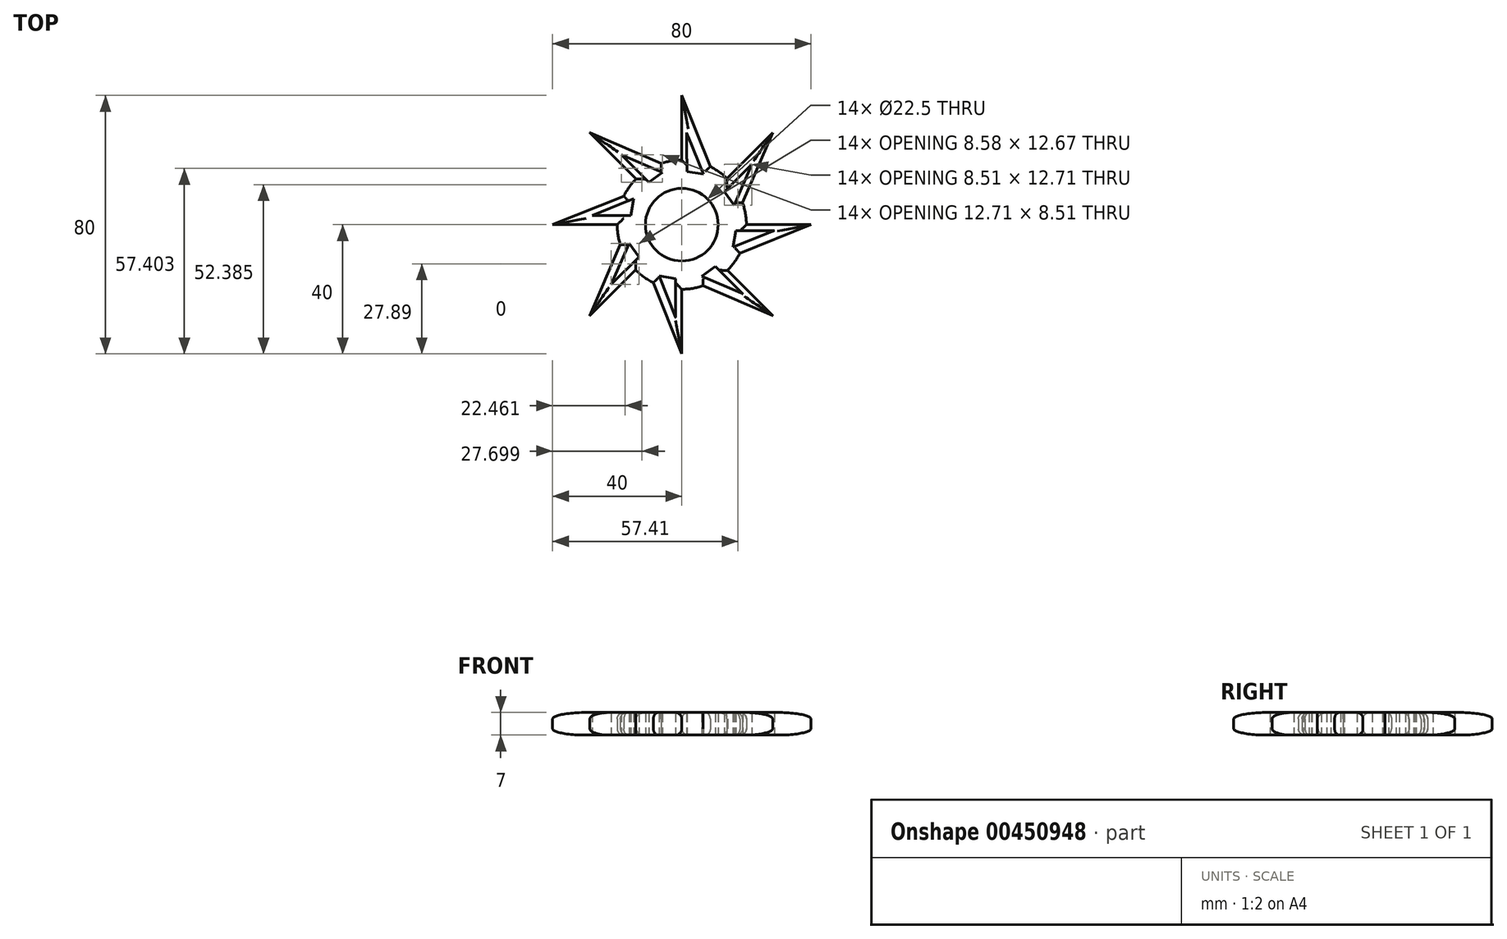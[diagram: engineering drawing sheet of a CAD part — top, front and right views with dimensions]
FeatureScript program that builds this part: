
annotation { "Feature Type Name" : "Feature", "Feature Type Description" : "" }
export const myFeature = defineFeature(function(context is Context, id is Id, definition is map)
    precondition{}
    {
        {
            var Q0;
            Q0=qCreatedBy(makeId("Top.planeOp"),FACE);
            var sketch = newSketch(context, id + "F0", { "sketchPlane" : qUnion([Q0])});
            skCircle(sketch, "E0", {"center": v(0, 0) * mm, "radius": 16 * mm});
            skCircle(sketch, "E1", {"center": v(0, 0) * mm, "radius": 11.25 * mm});
            skCircle(sketch, "E2", {"center": v(0, 0) * mm, "radius": 40 * mm});
            skLineSegment(sketch, "E3", {"start": v(0, 16) * mm, "end": v(0, 40) * mm});
            skLineSegment(sketch, "E4", {"start": v(0, 40) * mm, "end": v(16, 0) * mm});
            skLineSegment(sketch, "E5", {"start": v(16, 0) * mm, "end": v(40, 0) * mm});
            skLineSegment(sketch, "E6", {"start": v(40, 0) * mm, "end": v(0, -16) * mm});
            skLineSegment(sketch, "E7", {"start": v(0, -16) * mm, "end": v(0, -40) * mm});
            skLineSegment(sketch, "E8", {"start": v(0, -40) * mm, "end": v(-16, 0) * mm});
            skLineSegment(sketch, "E9", {"start": v(-16, 0) * mm, "end": v(-40, 0) * mm});
            skLineSegment(sketch, "E10", {"start": v(-40, 0) * mm, "end": v(0, 16) * mm});
            skLineSegment(sketch, "E11", {"start": v(-11.48, 11.48) * mm, "end": v(-28.45, 28.45) * mm});
            skLineSegment(sketch, "E12", {"start": v(-28.45, 28.45) * mm, "end": v(11.15, 11.48) * mm});
            skLineSegment(sketch, "E13", {"start": v(11.15, 11.48) * mm, "end": v(28.12, 28.45) * mm});
            skLineSegment(sketch, "E14", {"start": v(28.12, 28.45) * mm, "end": v(11.15, -11.15) * mm});
            skLineSegment(sketch, "E15", {"start": v(11.15, -11.15) * mm, "end": v(28.12, -28.12) * mm});
            skLineSegment(sketch, "E16", {"start": v(28.12, -28.12) * mm, "end": v(-11.48, -11.15) * mm});
            skLineSegment(sketch, "E17", {"start": v(-11.48, -11.15) * mm, "end": v(-28.45, -28.12) * mm});
            skLineSegment(sketch, "E18", {"start": v(-28.45, -28.12) * mm, "end": v(-11.48, 11.48) * mm});
            skCircle(sketch, "E19", {"center": v(0, 0) * mm, "radius": 20 * mm});
            skLineSegment(sketch, "E20", {"start": v(-14.94, 8) * mm, "end": v(-27.78, 2.86) * mm});
            skPoint(sketch, "E20.startSnap0", {"position": v(-20, 8) * mm});
            skLineSegment(sketch, "E21", {"start": v(-27.78, 2.86) * mm, "end": v(-15.74, 2.86) * mm});
            skLineSegment(sketch, "E22", {"start": v(-15.74, 2.86) * mm, "end": v(-14.94, 8) * mm});
            skLineSegment(sketch, "E23", {"start": v(-5.94, 16.21) * mm, "end": v(-18.66, 21.66) * mm});
            skLineSegment(sketch, "E24", {"start": v(-18.66, 21.66) * mm, "end": v(-10.15, 13.15) * mm});
            skLineSegment(sketch, "E25", {"start": v(-10.15, 13.15) * mm, "end": v(-5.94, 16.21) * mm});
            skLineSegment(sketch, "E26", {"start": v(6.72, 15.65) * mm, "end": v(1.49, 28.45) * mm});
            skLineSegment(sketch, "E27", {"start": v(1.49, 28.45) * mm, "end": v(1.58, 16.42) * mm});
            skLineSegment(sketch, "E28", {"start": v(1.58, 16.42) * mm, "end": v(6.72, 15.65) * mm});
            skLineSegment(sketch, "E29", {"start": v(16.22, 6.03) * mm, "end": v(21.67, 18.74) * mm});
            skLineSegment(sketch, "E30", {"start": v(21.67, 18.74) * mm, "end": v(13.15, 10.23) * mm});
            skLineSegment(sketch, "E31", {"start": v(13.15, 10.23) * mm, "end": v(16.22, 6.03) * mm});
            skLineSegment(sketch, "E32", {"start": v(15.88, -6.94) * mm, "end": v(28.72, -1.8) * mm});
            skLineSegment(sketch, "E33", {"start": v(28.72, -1.8) * mm, "end": v(16.68, -1.8) * mm});
            skLineSegment(sketch, "E34", {"start": v(16.68, -1.8) * mm, "end": v(15.88, -6.94) * mm});
            skLineSegment(sketch, "E35", {"start": v(6.15, -15.96) * mm, "end": v(18.86, -21.4) * mm});
            skLineSegment(sketch, "E36", {"start": v(18.86, -21.4) * mm, "end": v(10.35, -12.9) * mm});
            skLineSegment(sketch, "E37", {"start": v(10.35, -12.9) * mm, "end": v(6.15, -15.96) * mm});
            skLineSegment(sketch, "E38", {"start": v(-7.01, -15.84) * mm, "end": v(-1.96, -28.72) * mm});
            skLineSegment(sketch, "E39", {"start": v(-1.96, -28.72) * mm, "end": v(-1.88, -16.68) * mm});
            skLineSegment(sketch, "E40", {"start": v(-1.88, -16.68) * mm, "end": v(-7.01, -15.84) * mm});
            skLineSegment(sketch, "E41", {"start": v(-16.28, -5.78) * mm, "end": v(-21.83, -18.44) * mm});
            skLineSegment(sketch, "E42", {"start": v(-21.83, -18.44) * mm, "end": v(-13.25, -10) * mm});
            skLineSegment(sketch, "E43", {"start": v(-13.25, -10) * mm, "end": v(-16.28, -5.78) * mm});
            skSolve(sketch);
        }
        {
            var Q0;
            {var subQ0=sQuery(id+"F0.wireOp",EDGE,"E14");var subQ1=sQuery(id+"F0.wireOp",EDGE,"E2");var subQ2=makeQuery(id+"F0.imprint","INTERSECT",VERTEX,{"derivedFrom":[subQ1,subQ0]});Q0=makeQuery(id+"F0.imprint","IMPRINT",FACE,{"disambiguationData":[TD([[makeQuery(id+"F0.imprint","IMPRINT",EDGE,{"disambiguationData":[TD([[subQ2,-1.0]])],"derivedFrom":subQ1}),-1.0]])]});}
            var Q1;
            {var subQ0=sQuery(id+"F0.wireOp",EDGE,"E12");var subQ1=sQuery(id+"F0.wireOp",EDGE,"E2");var subQ2=makeQuery(id+"F0.imprint","INTERSECT",VERTEX,{"derivedFrom":[subQ1,subQ0]});Q1=makeQuery(id+"F0.imprint","IMPRINT",FACE,{"disambiguationData":[TD([[makeQuery(id+"F0.imprint","IMPRINT",EDGE,{"disambiguationData":[TD([[subQ2,-1.0]])],"derivedFrom":subQ1}),-1.0]])]});}
            var Q2;
            {var subQ0=sQuery(id+"F0.wireOp",EDGE,"E19");var subQ5=sQuery(id+"F0.wireOp",EDGE,"E4");var subQ6=makeQuery(id+"F0.imprint","INTERSECT",VERTEX,{"derivedFrom":[subQ5,subQ0]});Q2=makeQuery(id+"F0.imprint","IMPRINT",FACE,{"disambiguationData":[TD([[makeQuery(id+"F0.imprint","IMPRINT",EDGE,{"disambiguationData":[TD([[subQ6,-1.0]])],"derivedFrom":subQ0}),-1.0]])]});}
            var Q3;
            {var subQ0=sQuery(id+"F0.wireOp",EDGE,"E19");var subQ1=sQuery(id+"F0.wireOp",EDGE,"E6");var subQ2=makeQuery(id+"F0.imprint","INTERSECT",VERTEX,{"derivedFrom":[subQ1,subQ0]});Q3=makeQuery(id+"F0.imprint","IMPRINT",FACE,{"disambiguationData":[TD([[makeQuery(id+"F0.imprint","IMPRINT",EDGE,{"disambiguationData":[TD([[subQ2,-1.0]])],"derivedFrom":subQ0}),-1.0]])]});}
            var Q4;
            {var subQ0=sQuery(id+"F0.wireOp",EDGE,"E19");var subQ1=sQuery(id+"F0.wireOp",EDGE,"E8");var subQ2=makeQuery(id+"F0.imprint","INTERSECT",VERTEX,{"derivedFrom":[subQ1,subQ0]});Q4=makeQuery(id+"F0.imprint","IMPRINT",FACE,{"disambiguationData":[TD([[makeQuery(id+"F0.imprint","IMPRINT",EDGE,{"disambiguationData":[TD([[subQ2,-1.0]])],"derivedFrom":subQ0}),-1.0]])]});}
            var Q5;
            {var subQ0=sQuery(id+"F0.wireOp",EDGE,"E19");var subQ1=sQuery(id+"F0.wireOp",EDGE,"E18");var subQ2=makeQuery(id+"F0.imprint","INTERSECT",VERTEX,{"derivedFrom":[subQ1,subQ0]});Q5=makeQuery(id+"F0.imprint","IMPRINT",FACE,{"disambiguationData":[TD([[makeQuery(id+"F0.imprint","IMPRINT",EDGE,{"disambiguationData":[TD([[subQ2,-1.0]])],"derivedFrom":subQ0}),-1.0]])]});}
            var Q6;
            {var subQ1=sQuery(id+"F0.wireOp",EDGE,"E14");var subQ6=sQuery(id+"F0.wireOp",EDGE,"E2");var subQ9=makeQuery(id+"F0.imprint","INTERSECT",VERTEX,{"derivedFrom":[subQ6,subQ1]});Q6=makeQuery(id+"F0.imprint","IMPRINT",FACE,{"disambiguationData":[TD([[makeQuery(id+"F0.imprint","IMPRINT",EDGE,{"disambiguationData":[TD([[subQ9,-1.0]])],"derivedFrom":subQ6}),1.0]])]});}
            var Q7;
            {var subQ1=sQuery(id+"F0.wireOp",EDGE,"E12");var subQ6=sQuery(id+"F0.wireOp",EDGE,"E2");var subQ9=makeQuery(id+"F0.imprint","INTERSECT",VERTEX,{"derivedFrom":[subQ6,subQ1]});Q7=makeQuery(id+"F0.imprint","IMPRINT",FACE,{"disambiguationData":[TD([[makeQuery(id+"F0.imprint","IMPRINT",EDGE,{"disambiguationData":[TD([[subQ9,-1.0]])],"derivedFrom":subQ6}),1.0]])]});}
            var Q8;
            {var subQ0=sQuery(id+"F0.wireOp",EDGE,"E19");var subQ1=sQuery(id+"F0.wireOp",EDGE,"E10");var subQ2=makeQuery(id+"F0.imprint","INTERSECT",VERTEX,{"derivedFrom":[subQ1,subQ0]});Q8=makeQuery(id+"F0.imprint","IMPRINT",FACE,{"disambiguationData":[TD([[makeQuery(id+"F0.imprint","IMPRINT",EDGE,{"disambiguationData":[TD([[subQ2,-1.0]])],"derivedFrom":subQ0}),-1.0]])]});}
            var Q9;
            {var subQ1=sQuery(id+"F0.wireOp",EDGE,"E15");var subQ5=sQuery(id+"F0.wireOp",EDGE,"E16");var subQ6=makeQuery(id+"F0.imprint","INTERSECT",VERTEX,{"derivedFrom":[subQ1,subQ5]});Q9=makeQuery(id+"F0.imprint","IMPRINT",FACE,{"disambiguationData":[TD([[makeQuery(id+"F0.imprint","IMPRINT",EDGE,{"disambiguationData":[TD([[subQ6,1.0]])],"derivedFrom":subQ1}),-1.0]])]});}
            var Q10;
            {var subQ5=sQuery(id+"F0.wireOp",EDGE,"E37");Q10=makeQuery(id+"F0.imprint","IMPRINT",FACE,{"disambiguationData":[TD([[makeQuery(id+"F0.imprint","IMPRINT",EDGE,{"derivedFrom":subQ5}),-1.0]])]});}
            var Q11;
            {var subQ0=sQuery(id+"F0.wireOp",EDGE,"E40");Q11=makeQuery(id+"F0.imprint","IMPRINT",FACE,{"disambiguationData":[TD([[makeQuery(id+"F0.imprint","IMPRINT",EDGE,{"derivedFrom":subQ0}),-1.0]])]});}
            var Q12;
            {var subQ0=sQuery(id+"F0.wireOp",EDGE,"E16");var subQ1=sQuery(id+"F0.wireOp",EDGE,"E7");var subQ2=makeQuery(id+"F0.imprint","INTERSECT",VERTEX,{"derivedFrom":[subQ1,subQ0]});Q12=makeQuery(id+"F0.imprint","IMPRINT",FACE,{"disambiguationData":[TD([[makeQuery(id+"F0.imprint","IMPRINT",EDGE,{"disambiguationData":[TD([[subQ2,-1.0]])],"derivedFrom":subQ1}),1.0]])]});}
            var Q13;
            {var subQ0=sQuery(id+"F0.wireOp",EDGE,"E19");var subQ1=sQuery(id+"F0.wireOp",EDGE,"E6");var subQ2=makeQuery(id+"F0.imprint","INTERSECT",VERTEX,{"derivedFrom":[subQ1,subQ0]});Q13=makeQuery(id+"F0.imprint","IMPRINT",FACE,{"disambiguationData":[TD([[makeQuery(id+"F0.imprint","IMPRINT",EDGE,{"disambiguationData":[TD([[subQ2,-1.0]])],"derivedFrom":subQ1}),1.0]])]});}
            var Q14;
            {var subQ1=sQuery(id+"F0.wireOp",EDGE,"E0");var subQ3=sQuery(id+"F0.wireOp",EDGE,"E14");var subQ4=makeQuery(id+"F0.imprint","INTERSECT",VERTEX,{"derivedFrom":[subQ1,subQ3]});Q14=makeQuery(id+"F0.imprint","IMPRINT",FACE,{"disambiguationData":[TD([[makeQuery(id+"F0.imprint","IMPRINT",EDGE,{"disambiguationData":[TD([[subQ4,1.0]])],"derivedFrom":subQ3}),1.0]])]});}
            var Q15;
            {var subQ3=sQuery(id+"F0.wireOp",EDGE,"E15");var subQ5=sQuery(id+"F0.wireOp",EDGE,"E14");var subQ7=makeQuery(id+"F0.imprint","INTERSECT",VERTEX,{"derivedFrom":[subQ5,subQ3]});Q15=makeQuery(id+"F0.imprint","IMPRINT",FACE,{"disambiguationData":[TD([[makeQuery(id+"F0.imprint","IMPRINT",EDGE,{"disambiguationData":[TD([[subQ7,1.0]])],"derivedFrom":subQ5}),1.0]])]});}
            var Q16;
            {var subQ0=sQuery(id+"F0.wireOp",EDGE,"E6");var subQ1=sQuery(id+"F0.wireOp",EDGE,"E0");var subQ3=makeQuery(id+"F0.imprint","INTERSECT",VERTEX,{"derivedFrom":[subQ1,subQ0]});Q16=makeQuery(id+"F0.imprint","IMPRINT",FACE,{"disambiguationData":[TD([[makeQuery(id+"F0.imprint","IMPRINT",EDGE,{"disambiguationData":[TD([[subQ3,1.0]])],"derivedFrom":subQ1}),1.0]])]});}
            var Q17;
            {var subQ0=sQuery(id+"F0.wireOp",EDGE,"E16");var subQ1=sQuery(id+"F0.wireOp",EDGE,"E0");var subQ2=makeQuery(id+"F0.imprint","INTERSECT",VERTEX,{"disambiguationData":[OD(0.0)],"derivedFrom":[subQ1,subQ0]});Q17=makeQuery(id+"F0.imprint","IMPRINT",FACE,{"disambiguationData":[TD([[makeQuery(id+"F0.imprint","IMPRINT",EDGE,{"disambiguationData":[TD([[subQ2,-1.0]])],"derivedFrom":subQ1}),1.0]])]});}
            var Q18;
            {var subQ0=sQuery(id+"F0.wireOp",EDGE,"E19");var subQ1=sQuery(id+"F0.wireOp",EDGE,"E8");var subQ2=makeQuery(id+"F0.imprint","INTERSECT",VERTEX,{"derivedFrom":[subQ1,subQ0]});Q18=makeQuery(id+"F0.imprint","IMPRINT",FACE,{"disambiguationData":[TD([[makeQuery(id+"F0.imprint","IMPRINT",EDGE,{"disambiguationData":[TD([[subQ2,-1.0]])],"derivedFrom":subQ1}),1.0]])]});}
            var Q19;
            {var subQ0=sQuery(id+"F0.wireOp",EDGE,"E18");var subQ1=sQuery(id+"F0.wireOp",EDGE,"E9");var subQ2=makeQuery(id+"F0.imprint","INTERSECT",VERTEX,{"derivedFrom":[subQ1,subQ0]});Q19=makeQuery(id+"F0.imprint","IMPRINT",FACE,{"disambiguationData":[TD([[makeQuery(id+"F0.imprint","IMPRINT",EDGE,{"disambiguationData":[TD([[subQ2,-1.0]])],"derivedFrom":subQ1}),1.0]])]});}
            var Q20;
            {var subQ0=sQuery(id+"F0.wireOp",EDGE,"E19");var subQ1=sQuery(id+"F0.wireOp",EDGE,"E10");var subQ2=makeQuery(id+"F0.imprint","INTERSECT",VERTEX,{"derivedFrom":[subQ1,subQ0]});Q20=makeQuery(id+"F0.imprint","IMPRINT",FACE,{"disambiguationData":[TD([[makeQuery(id+"F0.imprint","IMPRINT",EDGE,{"disambiguationData":[TD([[subQ2,-1.0]])],"derivedFrom":subQ1}),1.0]])]});}
            var Q21;
            {var subQ0=sQuery(id+"F0.wireOp",EDGE,"E12");var subQ1=sQuery(id+"F0.wireOp",EDGE,"E3");var subQ2=makeQuery(id+"F0.imprint","INTERSECT",VERTEX,{"derivedFrom":[subQ1,subQ0]});Q21=makeQuery(id+"F0.imprint","IMPRINT",FACE,{"disambiguationData":[TD([[makeQuery(id+"F0.imprint","IMPRINT",EDGE,{"disambiguationData":[TD([[subQ2,-1.0]])],"derivedFrom":subQ1}),1.0]])]});}
            var Q22;
            {var subQ0=sQuery(id+"F0.wireOp",EDGE,"E19");var subQ1=sQuery(id+"F0.wireOp",EDGE,"E4");var subQ2=makeQuery(id+"F0.imprint","INTERSECT",VERTEX,{"derivedFrom":[subQ1,subQ0]});Q22=makeQuery(id+"F0.imprint","IMPRINT",FACE,{"disambiguationData":[TD([[makeQuery(id+"F0.imprint","IMPRINT",EDGE,{"disambiguationData":[TD([[subQ2,-1.0]])],"derivedFrom":subQ1}),1.0]])]});}
            var Q23;
            {var subQ0=sQuery(id+"F0.wireOp",EDGE,"E12");var subQ1=sQuery(id+"F0.wireOp",EDGE,"E0");var subQ2=makeQuery(id+"F0.imprint","INTERSECT",VERTEX,{"disambiguationData":[OD(0.0)],"derivedFrom":[subQ1,subQ0]});Q23=makeQuery(id+"F0.imprint","IMPRINT",FACE,{"disambiguationData":[TD([[makeQuery(id+"F0.imprint","IMPRINT",EDGE,{"disambiguationData":[TD([[subQ2,-1.0]])],"derivedFrom":subQ1}),1.0]])]});}
            var Q24;
            {var subQ0=sQuery(id+"F0.wireOp",EDGE,"E14");var subQ1=sQuery(id+"F0.wireOp",EDGE,"E0");var subQ2=makeQuery(id+"F0.imprint","INTERSECT",VERTEX,{"derivedFrom":[subQ1,subQ0]});Q24=makeQuery(id+"F0.imprint","IMPRINT",FACE,{"disambiguationData":[TD([[makeQuery(id+"F0.imprint","IMPRINT",EDGE,{"disambiguationData":[TD([[subQ2,-1.0]])],"derivedFrom":subQ1}),1.0]])]});}
            var Q25;
            {var subQ0=sQuery(id+"F0.wireOp",EDGE,"E10");var subQ1=sQuery(id+"F0.wireOp",EDGE,"E0");var subQ3=makeQuery(id+"F0.imprint","INTERSECT",VERTEX,{"derivedFrom":[subQ1,subQ0]});Q25=makeQuery(id+"F0.imprint","IMPRINT",FACE,{"disambiguationData":[TD([[makeQuery(id+"F0.imprint","IMPRINT",EDGE,{"disambiguationData":[TD([[subQ3,1.0]])],"derivedFrom":subQ1}),1.0]])]});}
            var Q26;
            {var subQ0=sQuery(id+"F0.wireOp",EDGE,"E0");var subQ2=sQuery(id+"F0.wireOp",EDGE,"E18");var subQ3=makeQuery(id+"F0.imprint","INTERSECT",VERTEX,{"disambiguationData":[OD(0.0)],"derivedFrom":[subQ0,subQ2]});Q26=makeQuery(id+"F0.imprint","IMPRINT",FACE,{"disambiguationData":[TD([[makeQuery(id+"F0.imprint","IMPRINT",EDGE,{"disambiguationData":[TD([[subQ3,1.0]])],"derivedFrom":subQ2}),1.0]])]});}
            var Q27;
            {var subQ0=sQuery(id+"F0.wireOp",EDGE,"E8");var subQ1=sQuery(id+"F0.wireOp",EDGE,"E0");var subQ3=makeQuery(id+"F0.imprint","INTERSECT",VERTEX,{"derivedFrom":[subQ1,subQ0]});Q27=makeQuery(id+"F0.imprint","IMPRINT",FACE,{"disambiguationData":[TD([[makeQuery(id+"F0.imprint","IMPRINT",EDGE,{"disambiguationData":[TD([[subQ3,1.0]])],"derivedFrom":subQ1}),1.0]])]});}
            var Q28;
            {var subQ1=sQuery(id+"F0.wireOp",EDGE,"E0");var subQ3=sQuery(id+"F0.wireOp",EDGE,"E18");var subQ4=makeQuery(id+"F0.imprint","INTERSECT",VERTEX,{"disambiguationData":[OD(1.0)],"derivedFrom":[subQ1,subQ3]});Q28=makeQuery(id+"F0.imprint","IMPRINT",FACE,{"disambiguationData":[TD([[makeQuery(id+"F0.imprint","IMPRINT",EDGE,{"disambiguationData":[TD([[subQ4,1.0]])],"derivedFrom":subQ3}),-1.0]])]});}
            var Q29;
            Q29=makeQuery(id+"F0.imprint","IMPRINT",FACE,{"disambiguationData":[TD([[makeQuery(id+"F0.imprint","IMPRINT",EDGE,{"derivedFrom":sQuery(id+"F0.wireOp",EDGE,"E1")}),-1.0]])]});
            var Q30;
            {var subQ0=sQuery(id+"F0.wireOp",EDGE,"E8");var subQ1=sQuery(id+"F0.wireOp",EDGE,"E0");var subQ2=makeQuery(id+"F0.imprint","INTERSECT",VERTEX,{"derivedFrom":[subQ1,subQ0]});Q30=makeQuery(id+"F0.imprint","IMPRINT",FACE,{"disambiguationData":[TD([[makeQuery(id+"F0.imprint","IMPRINT",EDGE,{"disambiguationData":[TD([[subQ2,-1.0]])],"derivedFrom":subQ1}),-1.0]])]});}
            var Q31;
            {var subQ1=sQuery(id+"F0.wireOp",EDGE,"E0");var subQ3=sQuery(id+"F0.wireOp",EDGE,"E16");var subQ4=makeQuery(id+"F0.imprint","INTERSECT",VERTEX,{"disambiguationData":[OD(1.0)],"derivedFrom":[subQ1,subQ3]});Q31=makeQuery(id+"F0.imprint","IMPRINT",FACE,{"disambiguationData":[TD([[makeQuery(id+"F0.imprint","IMPRINT",EDGE,{"disambiguationData":[TD([[subQ4,1.0]])],"derivedFrom":subQ3}),-1.0]])]});}
            var Q32;
            {var subQ0=sQuery(id+"F0.wireOp",EDGE,"E6");var subQ1=sQuery(id+"F0.wireOp",EDGE,"E0");var subQ2=makeQuery(id+"F0.imprint","INTERSECT",VERTEX,{"derivedFrom":[subQ1,subQ0]});Q32=makeQuery(id+"F0.imprint","IMPRINT",FACE,{"disambiguationData":[TD([[makeQuery(id+"F0.imprint","IMPRINT",EDGE,{"disambiguationData":[TD([[subQ2,-1.0]])],"derivedFrom":subQ1}),-1.0]])]});}
            var Q33;
            {var subQ1=sQuery(id+"F0.wireOp",EDGE,"E0");var subQ3=sQuery(id+"F0.wireOp",EDGE,"E14");var subQ4=makeQuery(id+"F0.imprint","INTERSECT",VERTEX,{"derivedFrom":[subQ1,subQ3]});Q33=makeQuery(id+"F0.imprint","IMPRINT",FACE,{"disambiguationData":[TD([[makeQuery(id+"F0.imprint","IMPRINT",EDGE,{"disambiguationData":[TD([[subQ4,-1.0]])],"derivedFrom":subQ3}),1.0]])]});}
            var Q34;
            {var subQ0=sQuery(id+"F0.wireOp",EDGE,"E4");var subQ1=sQuery(id+"F0.wireOp",EDGE,"E0");var subQ2=makeQuery(id+"F0.imprint","INTERSECT",VERTEX,{"derivedFrom":[subQ1,subQ0]});Q34=makeQuery(id+"F0.imprint","IMPRINT",FACE,{"disambiguationData":[TD([[makeQuery(id+"F0.imprint","IMPRINT",EDGE,{"disambiguationData":[TD([[subQ2,-1.0]])],"derivedFrom":subQ1}),-1.0]])]});}
            var Q35;
            {var subQ14=sQuery(id+"F0.wireOp",EDGE,"E34");Q35=makeQuery(id+"F0.imprint","IMPRINT",FACE,{"disambiguationData":[TD([[makeQuery(id+"F0.imprint","IMPRINT",EDGE,{"derivedFrom":subQ14}),-1.0]])]});}
            var Q36;
            {var subQ12=sQuery(id+"F0.wireOp",EDGE,"E31");Q36=makeQuery(id+"F0.imprint","IMPRINT",FACE,{"disambiguationData":[TD([[makeQuery(id+"F0.imprint","IMPRINT",EDGE,{"derivedFrom":subQ12}),-1.0]])]});}
            var Q37;
            {var subQ10=sQuery(id+"F0.wireOp",EDGE,"E43");Q37=makeQuery(id+"F0.imprint","IMPRINT",FACE,{"disambiguationData":[TD([[makeQuery(id+"F0.imprint","IMPRINT",EDGE,{"derivedFrom":subQ10}),-1.0]])]});}
            var Q38;
            {var subQ1=sQuery(id+"F0.wireOp",EDGE,"E9");var subQ5=sQuery(id+"F0.wireOp",EDGE,"E18");var subQ8=makeQuery(id+"F0.imprint","INTERSECT",VERTEX,{"derivedFrom":[subQ1,subQ5]});Q38=makeQuery(id+"F0.imprint","IMPRINT",FACE,{"disambiguationData":[TD([[makeQuery(id+"F0.imprint","IMPRINT",EDGE,{"disambiguationData":[TD([[subQ8,-1.0]])],"derivedFrom":subQ1}),-1.0]])]});}
            var Q39;
            {var subQ9=sQuery(id+"F0.wireOp",EDGE,"E22");Q39=makeQuery(id+"F0.imprint","IMPRINT",FACE,{"disambiguationData":[TD([[makeQuery(id+"F0.imprint","IMPRINT",EDGE,{"derivedFrom":subQ9}),-1.0]])]});}
            var Q40;
            {var subQ0=sQuery(id+"F0.wireOp",EDGE,"E25");Q40=makeQuery(id+"F0.imprint","IMPRINT",FACE,{"disambiguationData":[TD([[makeQuery(id+"F0.imprint","IMPRINT",EDGE,{"derivedFrom":subQ0}),-1.0]])]});}
            var Q41;
            {var subQ0=sQuery(id+"F0.wireOp",EDGE,"E28");Q41=makeQuery(id+"F0.imprint","IMPRINT",FACE,{"disambiguationData":[TD([[makeQuery(id+"F0.imprint","IMPRINT",EDGE,{"derivedFrom":subQ0}),-1.0]])]});}
            var Q42;
            {var subQ0=sQuery(id+"F0.wireOp",EDGE,"E10");var subQ1=sQuery(id+"F0.wireOp",EDGE,"E0");var subQ2=makeQuery(id+"F0.imprint","INTERSECT",VERTEX,{"derivedFrom":[subQ1,subQ0]});Q42=makeQuery(id+"F0.imprint","IMPRINT",FACE,{"disambiguationData":[TD([[makeQuery(id+"F0.imprint","IMPRINT",EDGE,{"disambiguationData":[TD([[subQ2,-1.0]])],"derivedFrom":subQ1}),-1.0]])]});}
            var Q43;
            {var subQ1=sQuery(id+"F0.wireOp",EDGE,"E0");var subQ3=sQuery(id+"F0.wireOp",EDGE,"E12");var subQ4=makeQuery(id+"F0.imprint","INTERSECT",VERTEX,{"disambiguationData":[OD(1.0)],"derivedFrom":[subQ1,subQ3]});Q43=makeQuery(id+"F0.imprint","IMPRINT",FACE,{"disambiguationData":[TD([[makeQuery(id+"F0.imprint","IMPRINT",EDGE,{"disambiguationData":[TD([[subQ4,1.0]])],"derivedFrom":subQ3}),-1.0]])]});}
            extrude(context, id + "F1", {"entities" : qUnion([Q0, Q1, Q2, Q3, Q4, Q5, Q6, Q7, Q8, Q9, Q10, Q11, Q12, Q13, Q14, Q15, Q16, Q17, Q18, Q19, Q20, Q21, Q22, Q23, Q24, Q25, Q26, Q27, Q28, Q29, Q30, Q31, Q32, Q33, Q34, Q35, Q36, Q37, Q38, Q39, Q40, Q41, Q42, Q43]), "depth" : 7 * mm});
        }
        {
            var Q0;
            {var subQ0=sQuery(id+"F0.wireOp",EDGE,"E19");Q0=makeQuery(id+"F1.opExtrude","CAP_EDGE",EDGE,{"disambiguationData":[OSD([subQ0]),TDD([makeQuery(id+"F0.imprint","IMPRINT",EDGE,{"disambiguationData":[TD([[makeQuery(id+"F0.imprint","INTERSECT",VERTEX,{"derivedFrom":[sQuery(id+"F0.wireOp",EDGE,"E7"),subQ0]}),-1.0]])],"derivedFrom":subQ0})])],"isStart":false});}
            var Q1;
            Q1=makeQuery(id+"F1.opExtrude","CAP_EDGE",EDGE,{"disambiguationData":[OSD([sQuery(id+"F0.wireOp",EDGE,"E16")])],"isStart":false});
            var Q2;
            Q2=makeQuery(id+"F1.opExtrude","CAP_EDGE",EDGE,{"disambiguationData":[OSD([sQuery(id+"F0.wireOp",EDGE,"E15")])],"isStart":false});
            var Q3;
            {var subQ0=sQuery(id+"F0.wireOp",EDGE,"E19");Q3=makeQuery(id+"F1.opExtrude","CAP_EDGE",EDGE,{"disambiguationData":[OSD([subQ0]),TDD([makeQuery(id+"F0.imprint","IMPRINT",EDGE,{"disambiguationData":[TD([[makeQuery(id+"F0.imprint","INTERSECT",VERTEX,{"derivedFrom":[sQuery(id+"F0.wireOp",EDGE,"E6"),subQ0]}),1.0]])],"derivedFrom":subQ0})])],"isStart":false});}
            var Q4;
            Q4=makeQuery(id+"F1.opExtrude","CAP_EDGE",EDGE,{"disambiguationData":[OSD([sQuery(id+"F0.wireOp",EDGE,"E6")])],"isStart":false});
            var Q5;
            Q5=makeQuery(id+"F1.opExtrude","CAP_EDGE",EDGE,{"disambiguationData":[OSD([sQuery(id+"F0.wireOp",EDGE,"E5")])],"isStart":false});
            var Q6;
            {var subQ0=sQuery(id+"F0.wireOp",EDGE,"E19");Q6=makeQuery(id+"F1.opExtrude","CAP_EDGE",EDGE,{"disambiguationData":[OSD([subQ0]),TDD([makeQuery(id+"F0.imprint","IMPRINT",EDGE,{"disambiguationData":[TD([[makeQuery(id+"F0.imprint","INTERSECT",VERTEX,{"derivedFrom":[sQuery(id+"F0.wireOp",EDGE,"E5"),subQ0]}),-1.0]])],"derivedFrom":subQ0})])],"isStart":false});}
            var Q7;
            Q7=makeQuery(id+"F1.opExtrude","CAP_EDGE",EDGE,{"disambiguationData":[OSD([sQuery(id+"F0.wireOp",EDGE,"E14")])],"isStart":false});
            var Q8;
            Q8=makeQuery(id+"F1.opExtrude","CAP_EDGE",EDGE,{"disambiguationData":[OSD([sQuery(id+"F0.wireOp",EDGE,"E13")])],"isStart":false});
            var Q9;
            {var subQ0=sQuery(id+"F0.wireOp",EDGE,"E19");Q9=makeQuery(id+"F1.opExtrude","CAP_EDGE",EDGE,{"disambiguationData":[OSD([subQ0]),TDD([makeQuery(id+"F0.imprint","IMPRINT",EDGE,{"disambiguationData":[TD([[makeQuery(id+"F0.imprint","INTERSECT",VERTEX,{"derivedFrom":[sQuery(id+"F0.wireOp",EDGE,"E4"),subQ0]}),1.0]])],"derivedFrom":subQ0})])],"isStart":false});}
            var Q10;
            Q10=makeQuery(id+"F1.opExtrude","CAP_EDGE",EDGE,{"disambiguationData":[OSD([sQuery(id+"F0.wireOp",EDGE,"E4")])],"isStart":false});
            var Q11;
            Q11=makeQuery(id+"F1.opExtrude","CAP_EDGE",EDGE,{"disambiguationData":[OSD([sQuery(id+"F0.wireOp",EDGE,"E3")])],"isStart":false});
            var Q12;
            {var subQ0=sQuery(id+"F0.wireOp",EDGE,"E19");Q12=makeQuery(id+"F1.opExtrude","CAP_EDGE",EDGE,{"disambiguationData":[OSD([subQ0]),TDD([makeQuery(id+"F0.imprint","IMPRINT",EDGE,{"disambiguationData":[TD([[makeQuery(id+"F0.imprint","INTERSECT",VERTEX,{"derivedFrom":[sQuery(id+"F0.wireOp",EDGE,"E3"),subQ0]}),-1.0]])],"derivedFrom":subQ0})])],"isStart":false});}
            var Q13;
            Q13=makeQuery(id+"F1.opExtrude","CAP_EDGE",EDGE,{"disambiguationData":[OSD([sQuery(id+"F0.wireOp",EDGE,"E12")])],"isStart":false});
            var Q14;
            Q14=makeQuery(id+"F1.opExtrude","CAP_EDGE",EDGE,{"disambiguationData":[OSD([sQuery(id+"F0.wireOp",EDGE,"E11")])],"isStart":false});
            var Q15;
            {var subQ0=sQuery(id+"F0.wireOp",EDGE,"E19");Q15=makeQuery(id+"F1.opExtrude","CAP_EDGE",EDGE,{"disambiguationData":[OSD([subQ0]),TDD([makeQuery(id+"F0.imprint","IMPRINT",EDGE,{"disambiguationData":[TD([[makeQuery(id+"F0.imprint","INTERSECT",VERTEX,{"derivedFrom":[sQuery(id+"F0.wireOp",EDGE,"E10"),subQ0]}),1.0]])],"derivedFrom":subQ0})])],"isStart":false});}
            var Q16;
            Q16=makeQuery(id+"F1.opExtrude","CAP_EDGE",EDGE,{"disambiguationData":[OSD([sQuery(id+"F0.wireOp",EDGE,"E10")])],"isStart":false});
            var Q17;
            Q17=makeQuery(id+"F1.opExtrude","CAP_EDGE",EDGE,{"disambiguationData":[OSD([sQuery(id+"F0.wireOp",EDGE,"E9")])],"isStart":false});
            var Q18;
            Q18=makeQuery(id+"F1.opExtrude","CAP_EDGE",EDGE,{"disambiguationData":[OSD([sQuery(id+"F0.wireOp",EDGE,"E18")])],"isStart":false});
            var Q19;
            Q19=makeQuery(id+"F1.opExtrude","CAP_EDGE",EDGE,{"disambiguationData":[OSD([sQuery(id+"F0.wireOp",EDGE,"E17")])],"isStart":false});
            var Q20;
            {var subQ0=sQuery(id+"F0.wireOp",EDGE,"E19");Q20=makeQuery(id+"F1.opExtrude","CAP_EDGE",EDGE,{"disambiguationData":[OSD([subQ0]),TDD([makeQuery(id+"F0.imprint","IMPRINT",EDGE,{"disambiguationData":[TD([[makeQuery(id+"F0.imprint","INTERSECT",VERTEX,{"derivedFrom":[sQuery(id+"F0.wireOp",EDGE,"E8"),subQ0]}),1.0]])],"derivedFrom":subQ0})])],"isStart":false});}
            var Q21;
            Q21=makeQuery(id+"F1.opExtrude","CAP_EDGE",EDGE,{"disambiguationData":[OSD([sQuery(id+"F0.wireOp",EDGE,"E8")])],"isStart":false});
            var Q22;
            Q22=makeQuery(id+"F1.opExtrude","CAP_EDGE",EDGE,{"disambiguationData":[OSD([sQuery(id+"F0.wireOp",EDGE,"E7")])],"isStart":false});
            var Q23;
            {var subQ0=sQuery(id+"F0.wireOp",EDGE,"E19");Q23=makeQuery(id+"F1.opExtrude","CAP_EDGE",EDGE,{"disambiguationData":[OSD([subQ0]),TDD([makeQuery(id+"F0.imprint","IMPRINT",EDGE,{"disambiguationData":[TD([[makeQuery(id+"F0.imprint","INTERSECT",VERTEX,{"derivedFrom":[sQuery(id+"F0.wireOp",EDGE,"E9"),subQ0]}),-1.0]])],"derivedFrom":subQ0})])],"isStart":false});}
            fillet(context, id + "F2", {"entities" : qUnion([Q0, Q1, Q2, Q3, Q4, Q5, Q6, Q7, Q8, Q9, Q10, Q11, Q12, Q13, Q14, Q15, Q16, Q17, Q18, Q19, Q20, Q21, Q22, Q23]), "radius" : 2 * mm, "tangentPropagation" : true, "allowEdgeOverflow" : false});
        }
        {
            var Q0;
            Q0=makeQuery(id+"F1.opExtrude","CAP_EDGE",EDGE,{"disambiguationData":[OSD([sQuery(id+"F0.wireOp",EDGE,"E16")])],"isStart":true});
            var Q1;
            {var subQ0=sQuery(id+"F0.wireOp",EDGE,"E19");Q1=makeQuery(id+"F1.opExtrude","CAP_EDGE",EDGE,{"disambiguationData":[OSD([subQ0]),TDD([makeQuery(id+"F0.imprint","IMPRINT",EDGE,{"disambiguationData":[TD([[makeQuery(id+"F0.imprint","INTERSECT",VERTEX,{"derivedFrom":[sQuery(id+"F0.wireOp",EDGE,"E7"),subQ0]}),-1.0]])],"derivedFrom":subQ0})])],"isStart":true});}
            var Q2;
            Q2=makeQuery(id+"F1.opExtrude","CAP_EDGE",EDGE,{"disambiguationData":[OSD([sQuery(id+"F0.wireOp",EDGE,"E7")])],"isStart":true});
            var Q3;
            Q3=makeQuery(id+"F1.opExtrude","CAP_EDGE",EDGE,{"disambiguationData":[OSD([sQuery(id+"F0.wireOp",EDGE,"E8")])],"isStart":true});
            var Q4;
            {var subQ0=sQuery(id+"F0.wireOp",EDGE,"E19");Q4=makeQuery(id+"F1.opExtrude","CAP_EDGE",EDGE,{"disambiguationData":[OSD([subQ0]),TDD([makeQuery(id+"F0.imprint","IMPRINT",EDGE,{"disambiguationData":[TD([[makeQuery(id+"F0.imprint","INTERSECT",VERTEX,{"derivedFrom":[sQuery(id+"F0.wireOp",EDGE,"E8"),subQ0]}),1.0]])],"derivedFrom":subQ0})])],"isStart":true});}
            var Q5;
            Q5=makeQuery(id+"F1.opExtrude","CAP_EDGE",EDGE,{"disambiguationData":[OSD([sQuery(id+"F0.wireOp",EDGE,"E17")])],"isStart":true});
            var Q6;
            Q6=makeQuery(id+"F1.opExtrude","CAP_EDGE",EDGE,{"disambiguationData":[OSD([sQuery(id+"F0.wireOp",EDGE,"E18")])],"isStart":true});
            var Q7;
            {var subQ0=sQuery(id+"F0.wireOp",EDGE,"E19");Q7=makeQuery(id+"F1.opExtrude","CAP_EDGE",EDGE,{"disambiguationData":[OSD([subQ0]),TDD([makeQuery(id+"F0.imprint","IMPRINT",EDGE,{"disambiguationData":[TD([[makeQuery(id+"F0.imprint","INTERSECT",VERTEX,{"derivedFrom":[sQuery(id+"F0.wireOp",EDGE,"E9"),subQ0]}),-1.0]])],"derivedFrom":subQ0})])],"isStart":true});}
            var Q8;
            Q8=makeQuery(id+"F1.opExtrude","CAP_EDGE",EDGE,{"disambiguationData":[OSD([sQuery(id+"F0.wireOp",EDGE,"E9")])],"isStart":true});
            var Q9;
            Q9=makeQuery(id+"F1.opExtrude","CAP_EDGE",EDGE,{"disambiguationData":[OSD([sQuery(id+"F0.wireOp",EDGE,"E10")])],"isStart":true});
            var Q10;
            {var subQ0=sQuery(id+"F0.wireOp",EDGE,"E19");Q10=makeQuery(id+"F1.opExtrude","CAP_EDGE",EDGE,{"disambiguationData":[OSD([subQ0]),TDD([makeQuery(id+"F0.imprint","IMPRINT",EDGE,{"disambiguationData":[TD([[makeQuery(id+"F0.imprint","INTERSECT",VERTEX,{"derivedFrom":[sQuery(id+"F0.wireOp",EDGE,"E10"),subQ0]}),1.0]])],"derivedFrom":subQ0})])],"isStart":true});}
            var Q11;
            Q11=makeQuery(id+"F1.opExtrude","CAP_EDGE",EDGE,{"disambiguationData":[OSD([sQuery(id+"F0.wireOp",EDGE,"E11")])],"isStart":true});
            var Q12;
            Q12=makeQuery(id+"F1.opExtrude","CAP_EDGE",EDGE,{"disambiguationData":[OSD([sQuery(id+"F0.wireOp",EDGE,"E12")])],"isStart":true});
            var Q13;
            {var subQ0=sQuery(id+"F0.wireOp",EDGE,"E19");Q13=makeQuery(id+"F1.opExtrude","CAP_EDGE",EDGE,{"disambiguationData":[OSD([subQ0]),TDD([makeQuery(id+"F0.imprint","IMPRINT",EDGE,{"disambiguationData":[TD([[makeQuery(id+"F0.imprint","INTERSECT",VERTEX,{"derivedFrom":[sQuery(id+"F0.wireOp",EDGE,"E3"),subQ0]}),-1.0]])],"derivedFrom":subQ0})])],"isStart":true});}
            var Q14;
            Q14=makeQuery(id+"F1.opExtrude","CAP_EDGE",EDGE,{"disambiguationData":[OSD([sQuery(id+"F0.wireOp",EDGE,"E3")])],"isStart":true});
            var Q15;
            Q15=makeQuery(id+"F1.opExtrude","CAP_EDGE",EDGE,{"disambiguationData":[OSD([sQuery(id+"F0.wireOp",EDGE,"E4")])],"isStart":true});
            var Q16;
            {var subQ0=sQuery(id+"F0.wireOp",EDGE,"E19");Q16=makeQuery(id+"F1.opExtrude","CAP_EDGE",EDGE,{"disambiguationData":[OSD([subQ0]),TDD([makeQuery(id+"F0.imprint","IMPRINT",EDGE,{"disambiguationData":[TD([[makeQuery(id+"F0.imprint","INTERSECT",VERTEX,{"derivedFrom":[sQuery(id+"F0.wireOp",EDGE,"E4"),subQ0]}),1.0]])],"derivedFrom":subQ0})])],"isStart":true});}
            var Q17;
            Q17=makeQuery(id+"F1.opExtrude","CAP_EDGE",EDGE,{"disambiguationData":[OSD([sQuery(id+"F0.wireOp",EDGE,"E13")])],"isStart":true});
            var Q18;
            Q18=makeQuery(id+"F1.opExtrude","CAP_EDGE",EDGE,{"disambiguationData":[OSD([sQuery(id+"F0.wireOp",EDGE,"E14")])],"isStart":true});
            var Q19;
            {var subQ0=sQuery(id+"F0.wireOp",EDGE,"E19");Q19=makeQuery(id+"F1.opExtrude","CAP_EDGE",EDGE,{"disambiguationData":[OSD([subQ0]),TDD([makeQuery(id+"F0.imprint","IMPRINT",EDGE,{"disambiguationData":[TD([[makeQuery(id+"F0.imprint","INTERSECT",VERTEX,{"derivedFrom":[sQuery(id+"F0.wireOp",EDGE,"E5"),subQ0]}),-1.0]])],"derivedFrom":subQ0})])],"isStart":true});}
            var Q20;
            Q20=makeQuery(id+"F1.opExtrude","CAP_EDGE",EDGE,{"disambiguationData":[OSD([sQuery(id+"F0.wireOp",EDGE,"E5")])],"isStart":true});
            var Q21;
            Q21=makeQuery(id+"F1.opExtrude","CAP_EDGE",EDGE,{"disambiguationData":[OSD([sQuery(id+"F0.wireOp",EDGE,"E6")])],"isStart":true});
            var Q22;
            {var subQ0=sQuery(id+"F0.wireOp",EDGE,"E19");Q22=makeQuery(id+"F1.opExtrude","CAP_EDGE",EDGE,{"disambiguationData":[OSD([subQ0]),TDD([makeQuery(id+"F0.imprint","IMPRINT",EDGE,{"disambiguationData":[TD([[makeQuery(id+"F0.imprint","INTERSECT",VERTEX,{"derivedFrom":[sQuery(id+"F0.wireOp",EDGE,"E6"),subQ0]}),1.0]])],"derivedFrom":subQ0})])],"isStart":true});}
            var Q23;
            Q23=makeQuery(id+"F1.opExtrude","CAP_EDGE",EDGE,{"disambiguationData":[OSD([sQuery(id+"F0.wireOp",EDGE,"E15")])],"isStart":true});
            fillet(context, id + "F3", {"entities" : qUnion([Q0, Q1, Q2, Q3, Q4, Q5, Q6, Q7, Q8, Q9, Q10, Q11, Q12, Q13, Q14, Q15, Q16, Q17, Q18, Q19, Q20, Q21, Q22, Q23]), "radius" : 2 * mm, "tangentPropagation" : true, "allowEdgeOverflow" : false});
        }
    });
